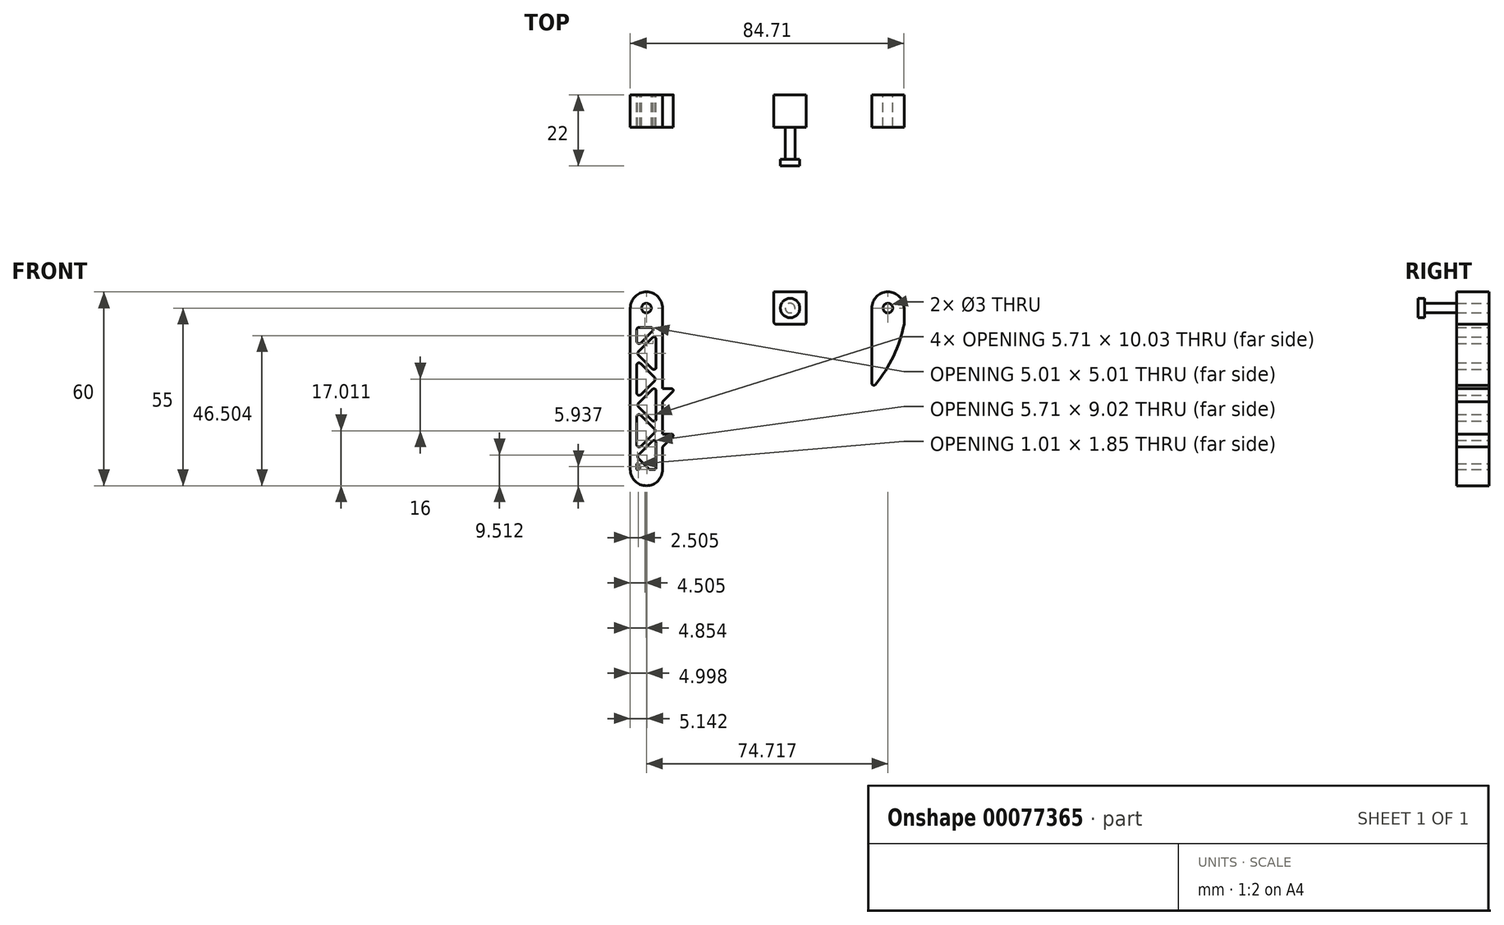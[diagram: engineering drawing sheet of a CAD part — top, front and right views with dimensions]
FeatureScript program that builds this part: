
annotation { "Feature Type Name" : "Feature", "Feature Type Description" : "" }
export const myFeature = defineFeature(function(context is Context, id is Id, definition is map)
    precondition{}
    {
        {
            var Q0;
            Q0=qCreatedBy(makeId("Front.planeOp"),FACE);
            var sketch = newSketch(context, id + "F0", { "sketchPlane" : qUnion([Q0])});
            skLineSegment(sketch, "E0.left", {"start": v(-59.36, 43) * mm, "end": v(-59.36, -7) * mm});
            skLineSegment(sketch, "E0.right", {"start": v(-49.36, 43) * mm, "end": v(-49.36, -7) * mm});
            skLineSegment(sketch, "E1", {"start": v(-54.36, 48) * mm, "end": v(-54.36, 38) * mm, "construction": true});
            skArc(sketch, "E2", {"start": v(-49.36, 43) * mm, "mid": v(-54.36, 48) * mm, "end": v(-59.36, 43) * mm});
            skArc(sketch, "E3", {"start": v(-59.36, -7) * mm, "mid": v(-54.36, -12) * mm, "end": v(-49.36, -7) * mm});
            skPoint(sketch, "E4.orphan", {"position": v(-49.36, 48) * mm});
            skPoint(sketch, "E5.orphan", {"position": v(-49.36, -12) * mm});
            skPoint(sketch, "E6.orphan", {"position": v(-59.36, -12) * mm});
            skPoint(sketch, "E7.orphan", {"position": v(-59.36, 48) * mm});
            skLineSegment(sketch, "E8", {"start": v(-57.36, -6.89) * mm, "end": v(-57.36, -5.24) * mm});
            skLineSegment(sketch, "E9", {"start": v(-56.67, 37.01) * mm, "end": v(-53.04, 37.01) * mm});
            skLineSegment(sketch, "E10", {"start": v(-51.36, -6.3) * mm, "end": v(-51.36, 1.33) * mm});
            skPoint(sketch, "E11", {"position": v(-51.36, 15) * mm});
            skPoint(sketch, "E12", {"position": v(-57.36, 15.01) * mm});
            skLineSegment(sketch, "E13", {"start": v(-57.36, 36.32) * mm, "end": v(-57.36, 32.69) * mm});
            skLineSegment(sketch, "E14", {"start": v(-56.17, 32.2) * mm, "end": v(-52.55, 35.82) * mm});
            skLineSegment(sketch, "E15", {"start": v(-56.87, 29.5) * mm, "end": v(-52.55, 33.82) * mm});
            skLineSegment(sketch, "E16", {"start": v(-51.36, 33.33) * mm, "end": v(-51.36, 24.69) * mm});
            skLineSegment(sketch, "E17", {"start": v(-56.87, 28.52) * mm, "end": v(-52.55, 24.2) * mm});
            skLineSegment(sketch, "E18", {"start": v(-56.17, 25.82) * mm, "end": v(-51.85, 21.5) * mm});
            skLineSegment(sketch, "E19", {"start": v(-57.36, 25.33) * mm, "end": v(-57.36, 16.69) * mm});
            skLineSegment(sketch, "E20", {"start": v(-56.17, 16.2) * mm, "end": v(-51.85, 20.52) * mm});
            skLineSegment(sketch, "E21", {"start": v(-52.55, 17.82) * mm, "end": v(-56.87, 13.5) * mm});
            skLineSegment(sketch, "E22", {"start": v(-56.87, 12.52) * mm, "end": v(-52.55, 8.2) * mm});
            skLineSegment(sketch, "E23", {"start": v(-51.85, 5.5) * mm, "end": v(-56.17, 9.82) * mm});
            skLineSegment(sketch, "E24", {"start": v(-51.85, 4.52) * mm, "end": v(-56.17, 0.2) * mm});
            skPoint(sketch, "E25.orphan", {"position": v(-54.36, -2) * mm});
            skPoint(sketch, "E26.start.orphan", {"position": v(-54.36, -12) * mm});
            skLineSegment(sketch, "E27", {"start": v(-52.55, 1.82) * mm, "end": v(-56.87, -2.5) * mm});
            skLineSegment(sketch, "E28", {"start": v(-56.87, -3.48) * mm, "end": v(-53.55, -6.8) * mm});
            skLineSegment(sketch, "E29", {"start": v(-53.06, -7) * mm, "end": v(-52.06, -7) * mm});
            skLineSegment(sketch, "E30", {"start": v(-57.18, -5.17) * mm, "end": v(-56.55, -5.8) * mm});
            skPoint(sketch, "E30.endSnap0", {"position": v(-55.36, -5) * mm});
            skLineSegment(sketch, "E31", {"start": v(-57.04, -6.99) * mm, "end": v(-57.26, -6.99) * mm});
            skCircle(sketch, "E32", {"center": v(-54.36, 43) * mm, "radius": 1.5 * mm});
            skLineSegment(sketch, "E33.trimOffspring", {"start": v(-57.36, 32.69) * mm, "end": v(-57.36, 36.32) * mm});
            skLineSegment(sketch, "E34.trimOffspring", {"start": v(-51.36, 24.69) * mm, "end": v(-51.36, 33.33) * mm});
            skLineSegment(sketch, "E35.trimOffspring", {"start": v(-57.36, 16.69) * mm, "end": v(-57.36, 25.33) * mm});
            skLineSegment(sketch, "E36.trimOffspring", {"start": v(-51.36, 8.69) * mm, "end": v(-51.36, 17.33) * mm});
            skLineSegment(sketch, "E37.trimOffspring", {"start": v(-57.36, 0.69) * mm, "end": v(-57.36, 9.33) * mm});
            skPoint(sketch, "E38.visualSharp", {"position": v(-57.36, 37.01) * mm});
            skArc(sketch, "E38.filletArc", {"start": v(-56.67, 37.01) * mm, "mid": v(-57.16, 36.8) * mm, "end": v(-57.36, 36.32) * mm});
            skPoint(sketch, "E39.visualSharp", {"position": v(-57.36, 31.01) * mm});
            skArc(sketch, "E39.filletArc", {"start": v(-57.36, 32.69) * mm, "mid": v(-56.93, 32.05) * mm, "end": v(-56.17, 32.2) * mm});
            skPoint(sketch, "E40.visualSharp", {"position": v(-51.36, 37.01) * mm});
            skArc(sketch, "E40.filletArc", {"start": v(-52.55, 35.82) * mm, "mid": v(-52.4, 36.58) * mm, "end": v(-53.04, 37.01) * mm});
            skPoint(sketch, "E41.visualSharp", {"position": v(-51.36, 35.01) * mm});
            skArc(sketch, "E41.filletArc", {"start": v(-51.36, 33.33) * mm, "mid": v(-51.8, 33.97) * mm, "end": v(-52.55, 33.82) * mm});
            skPoint(sketch, "E42.visualSharp", {"position": v(-51.36, 23.01) * mm});
            skArc(sketch, "E42.filletArc", {"start": v(-52.55, 24.2) * mm, "mid": v(-51.8, 24.05) * mm, "end": v(-51.36, 24.69) * mm});
            skPoint(sketch, "E43.visualSharp", {"position": v(-57.36, 29.01) * mm});
            skArc(sketch, "E43.filletArc", {"start": v(-56.87, 29.5) * mm, "mid": v(-57.07, 29.01) * mm, "end": v(-56.87, 28.52) * mm});
            skPoint(sketch, "E44.visualSharp", {"position": v(-57.36, 27.01) * mm});
            skArc(sketch, "E44.filletArc", {"start": v(-56.17, 25.82) * mm, "mid": v(-56.93, 25.97) * mm, "end": v(-57.36, 25.33) * mm});
            skPoint(sketch, "E45.visualSharp", {"position": v(-51.36, 21.01) * mm});
            skArc(sketch, "E45.filletArc", {"start": v(-51.85, 20.52) * mm, "mid": v(-51.65, 21.01) * mm, "end": v(-51.85, 21.5) * mm});
            skArc(sketch, "E46.filletArc", {"start": v(-57.36, 16.69) * mm, "mid": v(-56.93, 16.05) * mm, "end": v(-56.17, 16.2) * mm});
            skPoint(sketch, "E47.visualSharp", {"position": v(-51.36, 19.01) * mm});
            skArc(sketch, "E47.filletArc", {"start": v(-51.36, 17.33) * mm, "mid": v(-51.8, 17.97) * mm, "end": v(-52.55, 17.82) * mm});
            skPoint(sketch, "E48.visualSharp", {"position": v(-51.36, 7.01) * mm});
            skArc(sketch, "E48.filletArc", {"start": v(-52.55, 8.2) * mm, "mid": v(-51.8, 8.05) * mm, "end": v(-51.36, 8.69) * mm});
            skPoint(sketch, "E49.visualSharp", {"position": v(-57.36, 13.01) * mm});
            skArc(sketch, "E49.filletArc", {"start": v(-56.87, 13.5) * mm, "mid": v(-57.07, 13.01) * mm, "end": v(-56.87, 12.52) * mm});
            skPoint(sketch, "E50.visualSharp", {"position": v(-57.36, 11.01) * mm});
            skArc(sketch, "E50.filletArc", {"start": v(-56.17, 9.82) * mm, "mid": v(-56.93, 9.97) * mm, "end": v(-57.36, 9.33) * mm});
            skPoint(sketch, "E51.visualSharp", {"position": v(-51.36, 5.01) * mm});
            skArc(sketch, "E51.filletArc", {"start": v(-51.85, 4.52) * mm, "mid": v(-51.65, 5.01) * mm, "end": v(-51.85, 5.5) * mm});
            skPoint(sketch, "E52.visualSharp", {"position": v(-57.36, -0.99) * mm});
            skArc(sketch, "E52.filletArc", {"start": v(-57.36, 0.69) * mm, "mid": v(-56.93, 0.05) * mm, "end": v(-56.17, 0.2) * mm});
            skPoint(sketch, "E53.visualSharp", {"position": v(-51.36, 3.01) * mm});
            skArc(sketch, "E53.filletArc", {"start": v(-51.36, 1.33) * mm, "mid": v(-51.8, 1.97) * mm, "end": v(-52.55, 1.82) * mm});
            skPoint(sketch, "E54.visualSharp", {"position": v(-57.36, -2.99) * mm});
            skArc(sketch, "E54.filletArc", {"start": v(-56.87, -2.5) * mm, "mid": v(-57.07, -2.99) * mm, "end": v(-56.87, -3.48) * mm});
            skPoint(sketch, "E55.visualSharp", {"position": v(-53.35, -7) * mm});
            skArc(sketch, "E55.filletArc", {"start": v(-53.55, -6.8) * mm, "mid": v(-53.33, -6.95) * mm, "end": v(-53.06, -7) * mm});
            skPoint(sketch, "E56.visualSharp", {"position": v(-51.36, -7) * mm});
            skArc(sketch, "E56.filletArc", {"start": v(-52.06, -7) * mm, "mid": v(-51.57, -6.8) * mm, "end": v(-51.36, -6.3) * mm});
            skPoint(sketch, "E57.visualSharp", {"position": v(-55.36, -7) * mm});
            skArc(sketch, "E57.filletArc", {"start": v(-57.04, -6.99) * mm, "mid": v(-56.4, -6.56) * mm, "end": v(-56.55, -5.8) * mm});
            skPoint(sketch, "E58.visualSharp", {"position": v(-57.36, -4.99) * mm});
            skArc(sketch, "E58.filletArc", {"start": v(-57.18, -5.17) * mm, "mid": v(-57.3, -5.14) * mm, "end": v(-57.36, -5.24) * mm});
            skPoint(sketch, "E59.visualSharp", {"position": v(-57.36, -6.99) * mm});
            skArc(sketch, "E59.filletArc", {"start": v(-57.36, -6.89) * mm, "mid": v(-57.33, -6.96) * mm, "end": v(-57.26, -6.99) * mm});
            skLineSegment(sketch, "E60", {"start": v(-49.36, 18) * mm, "end": v(-46.57, 18) * mm});
            skLineSegment(sketch, "E61", {"start": v(-49.36, 18) * mm, "end": v(-49.36, 14) * mm});
            skLineSegment(sketch, "E62", {"start": v(-46.22, 17.15) * mm, "end": v(-49.36, 14) * mm});
            skLineSegment(sketch, "E63", {"start": v(-49.36, 14) * mm, "end": v(-49.36, 4) * mm});
            skLineSegment(sketch, "E64", {"start": v(-49.36, 4) * mm, "end": v(-46.57, 4) * mm});
            skLineSegment(sketch, "E65", {"start": v(-49.36, 4) * mm, "end": v(-49.36, 0) * mm});
            skLineSegment(sketch, "E66", {"start": v(-49.36, 0) * mm, "end": v(-46.22, 3.15) * mm});
            skPoint(sketch, "E67.visualSharp", {"position": v(-45.36, 18) * mm});
            skArc(sketch, "E67.filletArc", {"start": v(-46.22, 17.15) * mm, "mid": v(-46.1, 17.7) * mm, "end": v(-46.57, 18) * mm});
            skPoint(sketch, "E68.visualSharp", {"position": v(-45.36, 4) * mm});
            skArc(sketch, "E68.filletArc", {"start": v(-46.22, 3.15) * mm, "mid": v(-46.1, 3.7) * mm, "end": v(-46.57, 4) * mm});
            skLineSegment(sketch, "E69.bottom", {"start": v(-14.91, 48) * mm, "end": v(-4.91, 48) * mm});
            skPoint(sketch, "E69.middle", {"position": v(-9.91, 43) * mm});
            skCircle(sketch, "E70", {"center": v(-9.91, 43) * mm, "radius": 1.5 * mm});
            skLineSegment(sketch, "E71.left", {"start": v(25.35, 43) * mm, "end": v(25.35, 38) * mm});
            skLineSegment(sketch, "E71.right", {"start": v(15.35, 43) * mm, "end": v(15.35, 38) * mm});
            skPoint(sketch, "E71.middle", {"position": v(20.35, 43) * mm});
            skLineSegment(sketch, "E72.left", {"start": v(15.35, 38) * mm, "end": v(15.35, 19.76) * mm});
            skArc(sketch, "E73", {"start": v(16.51, 19.35) * mm, "mid": v(22.08, 28.13) * mm, "end": v(25.35, 38) * mm});
            skPoint(sketch, "E72.top.end.orphan", {"position": v(25.35, 18) * mm});
            skArc(sketch, "E74", {"start": v(25.35, 43) * mm, "mid": v(20.35, 48) * mm, "end": v(15.35, 43) * mm});
            skCircle(sketch, "E75", {"center": v(20.35, 43) * mm, "radius": 1.5 * mm});
            skPoint(sketch, "E76.orphan", {"position": v(25.35, 48) * mm});
            skLineSegment(sketch, "E77.bottom", {"start": v(-5.56, 38) * mm, "end": v(-14.26, 38) * mm});
            skLineSegment(sketch, "E77.left", {"start": v(-4.91, 38.65) * mm, "end": v(-4.91, 48) * mm});
            skLineSegment(sketch, "E78", {"start": v(-14.91, 48) * mm, "end": v(-14.91, 38.65) * mm});
            skPoint(sketch, "E79.visualSharp", {"position": v(15.35, 18) * mm});
            skArc(sketch, "E79.filletArc", {"start": v(15.35, 19.76) * mm, "mid": v(15.79, 19.15) * mm, "end": v(16.51, 19.35) * mm});
            skPoint(sketch, "E80.visualSharp", {"position": v(-14.91, 38) * mm});
            skArc(sketch, "E80.filletArc", {"start": v(-14.91, 38.65) * mm, "mid": v(-14.72, 38.2) * mm, "end": v(-14.26, 38) * mm});
            skPoint(sketch, "E81.visualSharp", {"position": v(-4.91, 38) * mm});
            skArc(sketch, "E81.filletArc", {"start": v(-5.56, 38) * mm, "mid": v(-5.1, 38.2) * mm, "end": v(-4.91, 38.65) * mm});
            skSolve(sketch);
        }
        {
            var Q0;
            Q0=makeQuery(id+"F0.imprint","IMPRINT",FACE,{"disambiguationData":[TD([[makeQuery(id+"F0.imprint","IMPRINT",EDGE,{"derivedFrom":sQuery(id+"F0.wireOp",EDGE,"E0.left")}),1.0]])]});
            var Q1;
            Q1=makeQuery(id+"F0.imprint","IMPRINT",FACE,{"disambiguationData":[TD([[makeQuery(id+"F0.imprint","IMPRINT",EDGE,{"derivedFrom":sQuery(id+"F0.wireOp",EDGE,"E60")}),-1.0]])]});
            var Q2;
            Q2=makeQuery(id+"F0.imprint","IMPRINT",FACE,{"disambiguationData":[TD([[makeQuery(id+"F0.imprint","IMPRINT",EDGE,{"derivedFrom":sQuery(id+"F0.wireOp",EDGE,"E64")}),-1.0]])]});
            extrude(context, id + "F1", {"entities" : qUnion([Q0, Q1, Q2]), "depth" : 10 * mm});
        }
        {
            var Q0;
            Q0=makeQuery(id+"F0.imprint","IMPRINT",FACE,{"disambiguationData":[TD([[makeQuery(id+"F0.imprint","IMPRINT",EDGE,{"derivedFrom":sQuery(id+"F0.wireOp",EDGE,"E71.left")}),-1.0]])]});
            var Q1;
            Q1=makeQuery(id+"F0.imprint","IMPRINT",FACE,{"disambiguationData":[TD([[makeQuery(id+"F0.imprint","IMPRINT",EDGE,{"derivedFrom":sQuery(id+"F0.wireOp",EDGE,"E69.bottom")}),-1.0]])]});
            extrude(context, id + "F2", {"entities" : qUnion([Q0, Q1]), "depth" : 10 * mm});
        }
        {
            var Q0;
            Q0=makeQuery(id+"F0.imprint","IMPRINT",FACE,{"disambiguationData":[TD([[makeQuery(id+"F0.imprint","IMPRINT",EDGE,{"derivedFrom":sQuery(id+"F0.wireOp",EDGE,"E70")}),1.0]])]});
            extrude(context, id + "F3", {"entities" : qUnion([Q0]), "operationType" : NewBodyOperationType.ADD, "depth" : 20 * mm});
        }
        {
            var Q0;
            Q0=makeQuery(id+"F3.opExtrude","CAP_FACE",FACE,{"disambiguationData":[OSD([sQuery(id+"F0.wireOp",EDGE,"E70")])],"isStart":false});
            var sketch = newSketch(context, id + "F4", { "sketchPlane" : qUnion([Q0])});
            skCircle(sketch, "E82", {"center": v(-9.91, 43) * mm, "radius": 3 * mm});
            skSolve(sketch);
        }
        {
            var Q0;
            Q0=makeQuery(id+"F4.imprint","IMPRINT",FACE,{"disambiguationData":[TD([[makeQuery(id+"F4.imprint","IMPRINT",EDGE,{"derivedFrom":makeQuery(id+"F3.opExtrude","CAP_EDGE",EDGE,{"disambiguationData":[OSD([sQuery(id+"F0.wireOp",EDGE,"E70")])],"isStart":false})}),1.0]])]});
            var Q1;
            Q1=makeQuery(id+"F4.imprint","IMPRINT",FACE,{"disambiguationData":[TD([[makeQuery(id+"F4.imprint","IMPRINT",EDGE,{"derivedFrom":sQuery(id+"F4.wireOp",EDGE,"E82")}),1.0]])]});
            extrude(context, id + "F5", {"entities" : qUnion([Q0, Q1]), "operationType" : NewBodyOperationType.ADD, "depth" : 2 * mm});
        }
    });
